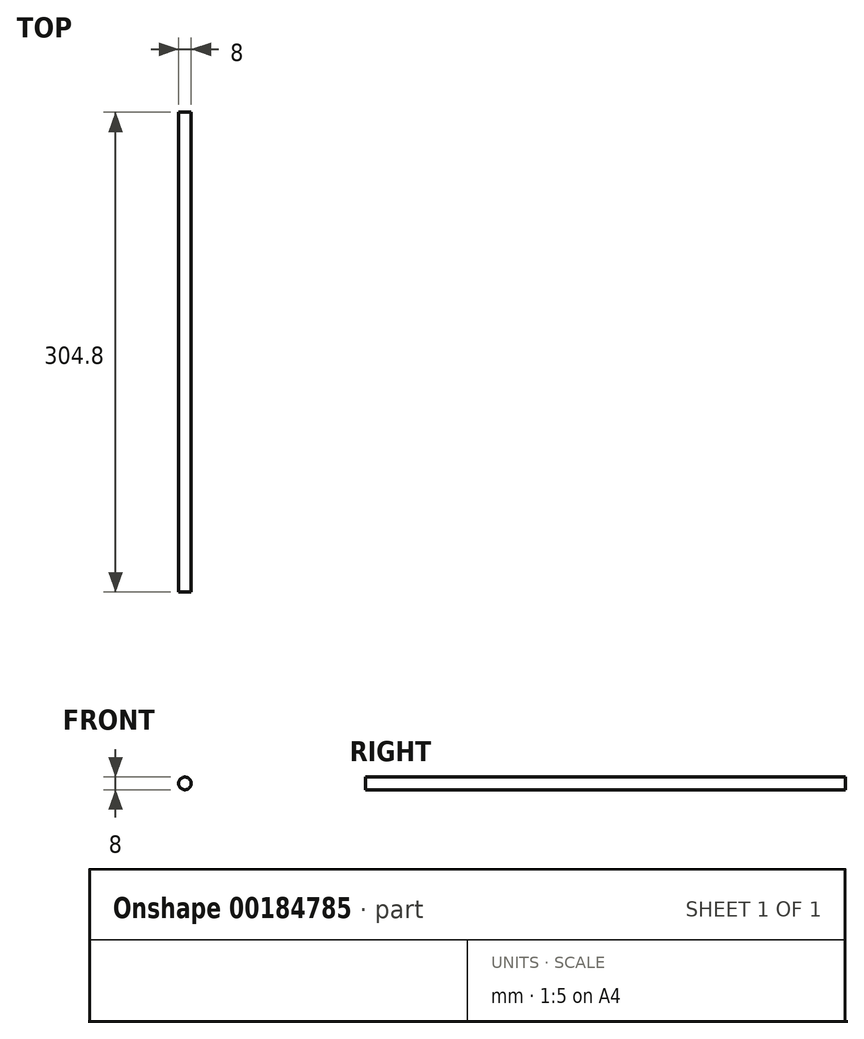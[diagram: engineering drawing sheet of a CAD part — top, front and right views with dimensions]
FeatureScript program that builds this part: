
annotation { "Feature Type Name" : "Feature", "Feature Type Description" : "" }
export const myFeature = defineFeature(function(context is Context, id is Id, definition is map)
    precondition{}
    {
        {
            var Q0;
            Q0=qCreatedBy(makeId("Front.planeOp"),FACE);
            var sketch = newSketch(context, id + "F0", { "sketchPlane" : qUnion([Q0])});
            skCircle(sketch, "E0", {"center": v(0, 0) * mm, "radius": 4 * mm});
            skSolve(sketch);
        }
        {
            var Q0;
            Q0=qSketchRegion(id+"F0",true);
            extrude(context, id + "F1", {"entities" : qUnion([Q0]), "oppositeDirection" : true, "depth" : 304.8 * mm});
        }
    });
